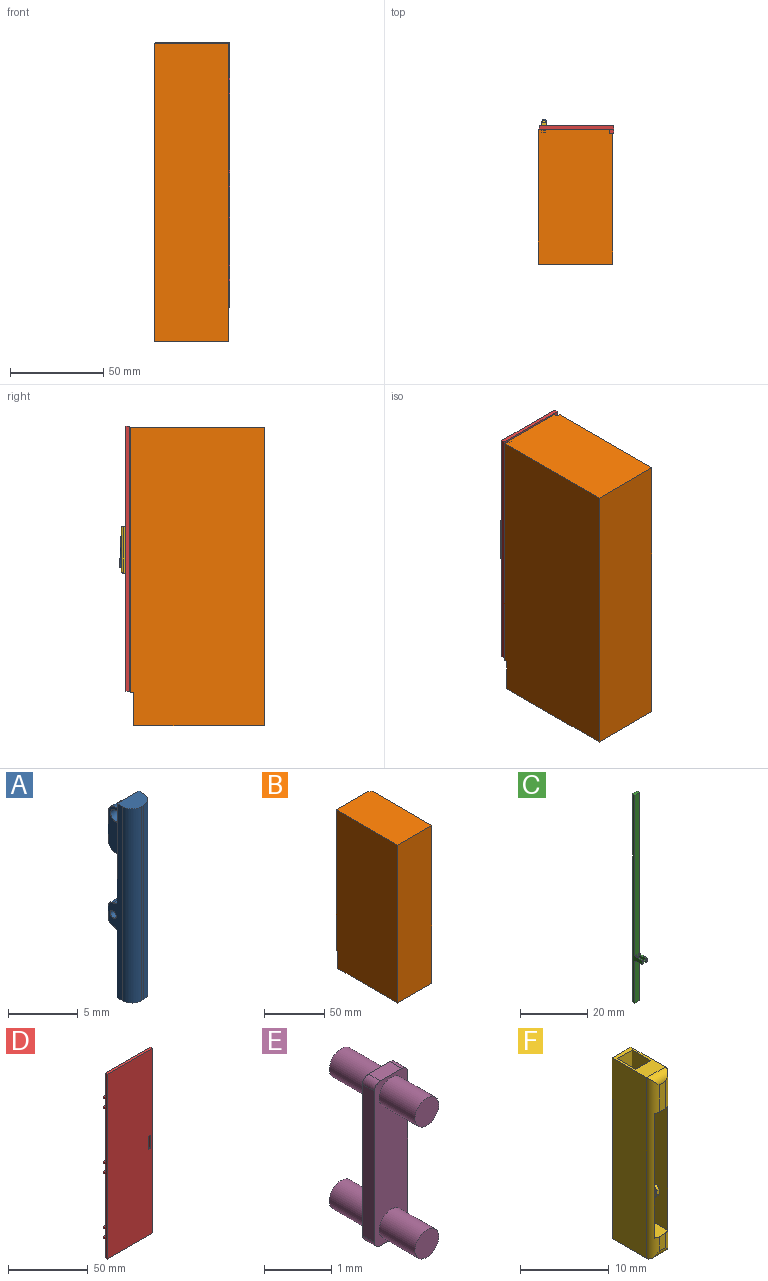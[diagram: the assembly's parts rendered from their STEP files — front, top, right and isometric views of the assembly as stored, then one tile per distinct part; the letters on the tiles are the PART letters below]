
ASSEMBLY  parts=6 mates=5
PART A: 31 faces, bbox 2.2x3x17 mm
  f0: plane 17x0.5mm, normal (1,0,0), area 8.5mm2, adj f2,f4,f29,f30
  f1: plane 17x0.5mm, normal (-1,0,0), area 8.5mm2, adj f2,f4,f28,f30
  f2: plane 2.2x1.5mm, normal (0,0,-1), area 2.9mm2, adj f0,f1,f3,f4,f28,f29
  f3: plane 17x0.2mm, normal (0,-1,0), area 3.4mm2, adj f2,f28,f29,f30
  f4: plane 17x2.2mm, normal (0,1,0), area 29.2mm2, adj f0,f1,f2,f5,f6,f8,f10,f12
  f5: plane 4.75x1.5mm, normal (-1,0,0), area 5mm2, adj f4,f7,f8,f9,f10,f11
  f6: plane 4.75x1.5mm, normal (1,0,0), area 5mm2, adj f4,f7,f8,f9,f10,f11
  f7: plane 2.5x1mm, normal (0,1,0), area 2.5mm2, adj f5,f6,f8,f9
  f8: cylinder r=0.75mm len=1.5mm, axis (-1,0,0), area 2.4mm2, adj f4,f5,f6,f7
  f9: cylinder r=0.75mm len=1mm, axis (1,0,0), area 1.2mm2, adj f5,f6,f7,f10
  f10: cylinder r=0.75mm len=1mm, axis (1,0,0), area 1.2mm2, adj f4,f5,f6,f9
  f11: cylinder r=0.5mm len=1mm, axis (1,0,0), area 3.1mm2, adj f5,f6
  f12: plane 3x1mm, normal (-1,0,0), area 1.7mm2, adj f4,f14,f19,f24,f25,f26,f27
  f13: plane 3x1mm, normal (1,0,0), area 1.7mm2, adj f4,f14,f19,f24,f25,f26,f27
  f14: plane 1x0.7mm, normal (0,1,0), area 0.7mm2, adj f12,f13,f24,f26
  f15: plane 3x1mm, normal (-1,0,0), area 1.7mm2, adj f4,f17,f18,f20,f21,f22,f23
  f16: plane 3x1mm, normal (1,0,0), area 1.7mm2, adj f4,f17,f18,f20,f21,f22,f23
  f17: plane 1x0.7mm, normal (0,1,0), area 0.7mm2, adj f15,f16,f20,f22
  f18: cylinder r=0.3mm len=0.7mm, axis (1,0,0), area 1.3mm2, adj f15,f16
  f19: cylinder r=0.3mm len=0.7mm, axis (1,0,0), area 1.3mm2, adj f12,f13
  f20: cylinder r=0.5mm len=0.7mm, axis (-1,0,0), area 0.5mm2, adj f15,f16,f17,f21
  f21: cylinder r=0.5mm len=0.7mm, axis (-1,0,0), area 0.5mm2, adj f4,f15,f16,f20
  f22: cylinder r=0.5mm len=0.7mm, axis (1,0,0), area 0.5mm2, adj f15,f16,f17,f23
  f23: cylinder r=0.5mm len=0.7mm, axis (1,0,0), area 0.5mm2, adj f4,f15,f16,f22
  f24: cylinder r=0.5mm len=0.7mm, axis (-1,0,0), area 0.5mm2, adj f12,f13,f14,f25
  f25: cylinder r=0.5mm len=0.7mm, axis (-1,0,0), area 0.5mm2, adj f4,f12,f13,f24
  f26: cylinder r=0.5mm len=0.7mm, axis (1,0,0), area 0.5mm2, adj f12,f13,f14,f27
  f27: cylinder r=0.5mm len=0.7mm, axis (1,0,0), area 0.5mm2, adj f4,f12,f13,f26
  f28: cylinder r=1mm len=17mm, axis (0,0,1), area 26.7mm2, adj f1,f2,f3,f30
  f29: cylinder r=1mm len=17mm, axis (0,0,-1), area 26.7mm2, adj f0,f2,f3,f30
  f30: plane 2.2x1.5mm, normal (0,0,1), area 2.9mm2, adj f0,f1,f3,f4,f28,f29
PART B: 38 faces, bbox 40x72x160 mm
  f0: plane 138x70mm, normal (1,0,0), area 9658mm2, adj f1,f12,f13,f35,f36,f37
  f1: plane 69x36mm, normal (0,0,-1), area 2484mm2, adj f0,f11,f13,f32,f36
  f2: plane 40x34mm, normal (0,1,0), area 739mm2, adj f6,f7,f10,f11,f21,f33,f34
  f3: plane 20x2mm, normal (0,1,0), area 40mm2, adj f6,f9,f11,f14,f32
  f4: plane 44x2mm, normal (0,1,0), area 88mm2, adj f6,f11,f18,f20
  f5: plane 44x2mm, normal (0,1,0), area 88mm2, adj f6,f11,f15,f17
  f6: plane 160x71.5mm, normal (1,0,0), area 11227mm2, adj f2,f3,f4,f5,f8,f9,f10,f14
  f7: plane 160x72mm, normal (-1,0,0), area 11484.7mm2, adj f2,f8,f9,f10,f34,f35
  f8: plane 160x40mm, normal (0,-1,0), area 6400mm2, adj f6,f7,f9,f10
  f9: plane 72x40mm, normal (0,0,1), area 2876mm2, adj f3,f6,f7,f8,f32,f35
  f10: plane 70x40mm, normal (0,0,-1), area 2800mm2, adj f2,f6,f7,f8
  f11: plane 138x69.5mm, normal (-1,0,0), area 9411mm2, adj f1,f2,f3,f4,f5,f12,f13,f14
  f12: plane 70x36mm, normal (0,0,1), area 2520mm2, adj f0,f11,f13,f33,f35
  f13: plane 138x36mm, normal (0,1,0), area 4968mm2, adj f0,f1,f11,f12
  f14: plane 2x2mm, normal (0,0,1), area 3.1mm2, adj f3,f6,f11,f16,f27,f28,f31
  f15: plane 2x2mm, normal (0,0,-1), area 3.1mm2, adj f5,f6,f11,f16,f27,f28,f31
  f16: plane 6x1mm, normal (0,1,0), area 6mm2, adj f14,f15,f27,f28
  f17: plane 2x2mm, normal (0,0,1), area 3.1mm2, adj f5,f6,f11,f19,f25,f26,f30
  f18: plane 2x2mm, normal (0,0,-1), area 3.1mm2, adj f4,f6,f11,f19,f25,f26,f30
  f19: plane 6x1mm, normal (0,1,0), area 6mm2, adj f17,f18,f25,f26
  f20: plane 2x2mm, normal (0,0,1), area 3.1mm2, adj f4,f6,f11,f22,f23,f24,f29
  f21: plane 2x2mm, normal (0,0,-1), area 3.1mm2, adj f2,f6,f11,f22,f23,f24,f29
  f22: plane 6x1mm, normal (0,1,0), area 6mm2, adj f20,f21,f23,f24
  f23: cylinder r=0.5mm len=6mm, axis (0,0,-1), area 4.7mm2, adj f6,f20,f21,f22
  f24: cylinder r=0.5mm len=6mm, axis (0,0,1), area 4.7mm2, adj f11,f20,f21,f22
  f25: cylinder r=0.5mm len=6mm, axis (0,0,-1), area 4.7mm2, adj f6,f17,f18,f19
  f26: cylinder r=0.5mm len=6mm, axis (0,0,1), area 4.7mm2, adj f11,f17,f18,f19
  f27: cylinder r=0.5mm len=6mm, axis (0,0,-1), area 4.7mm2, adj f6,f14,f15,f16
  f28: cylinder r=0.5mm len=6mm, axis (0,0,1), area 4.7mm2, adj f11,f14,f15,f16
  f29: cylinder r=0.5mm len=6mm, axis (0,0,1), area 18.8mm2, adj f20,f21
  f30: cylinder r=0.5mm len=6mm, axis (0,0,1), area 18.8mm2, adj f17,f18
  f31: cylinder r=0.5mm len=6mm, axis (0,0,1), area 18.8mm2, adj f14,f15
  f32: plane 4x2mm, normal (1,0,0), area 6mm2, adj f1,f3,f9,f35,f36,f37
  f33: plane 2.34x2mm, normal (1,0,0), area 4.7mm2, adj f2,f12,f34,f35
  f34: plane 38x2mm, normal (0,0,-1), area 76mm2, adj f2,f7,f33,f35
  f35: plane 142.34x38mm, normal (0,1,0), area 513mm2, adj f0,f7,f9,f12,f32,f33,f34,f37
  f36: plane 36x2mm, normal (0,-1,0), area 72mm2, adj f0,f1,f32,f37
  f37: plane 36x1mm, normal (0,0,-1), area 36mm2, adj f0,f32,f35,f36
PART C: 23 faces, bbox 2x4.3x76 mm
  f0: plane 76x2mm, normal (0,-1,0), area 149.8mm2, adj f1,f2,f3,f6,f9,f14,f15,f18
  f1: plane 76x4.25mm, normal (1,0,0), area 80.9mm2, adj f0,f3,f4,f5,f7,f8,f18,f19
  f2: plane 76x4.25mm, normal (-1,0,0), area 80.9mm2, adj f0,f3,f4,f10,f11,f12,f14,f15
  f3: plane 2x1mm, normal (0,0,-1), area 2mm2, adj f0,f1,f2,f4
  f4: plane 76x2mm, normal (0,1,0), area 152mm2, adj f1,f2,f3,f22
  f5: plane 2.25x0.45mm, normal (0,0,1), area 1mm2, adj f1,f6,f18,f20
  f6: plane 3.25x2.5mm, normal (-1,0,0), area 4.7mm2, adj f0,f5,f7,f8,f13,f18,f19,f20
  f7: plane 2.25x0.45mm, normal (0,0,-1), area 1mm2, adj f1,f6,f19,f21
  f8: plane 0.5x0.45mm, normal (0,-1,0), area 0.2mm2, adj f1,f6,f20,f21
  f9: plane 3.25x2.5mm, normal (1,0,0), area 4.7mm2, adj f0,f10,f11,f12,f13,f14,f15,f16
  f10: plane 2.25x0.45mm, normal (0,0,1), area 1mm2, adj f2,f9,f14,f16
  f11: plane 2.25x0.45mm, normal (0,0,-1), area 1mm2, adj f2,f9,f15,f17
  f12: plane 0.5x0.45mm, normal (0,-1,0), area 0.2mm2, adj f2,f9,f16,f17
  f13: cylinder r=0.25mm len=1.1mm, axis (-1,0,0), area 1.7mm2, adj f6,f9
  f14: cylinder r=0.5mm len=0.5mm, axis (-1,0,0), area 0.4mm2, adj f0,f2,f9,f10
  f15: cylinder r=0.5mm len=0.5mm, axis (1,0,0), area 0.4mm2, adj f0,f2,f9,f11
  f16: cylinder r=0.5mm len=0.5mm, axis (1,0,0), area 0.4mm2, adj f2,f9,f10,f12
  f17: cylinder r=0.5mm len=0.5mm, axis (-1,0,0), area 0.4mm2, adj f2,f9,f11,f12
  f18: cylinder r=0.5mm len=0.5mm, axis (-1,0,0), area 0.4mm2, adj f0,f1,f5,f6
  f19: cylinder r=0.5mm len=0.5mm, axis (1,0,0), area 0.4mm2, adj f0,f1,f6,f7
  f20: cylinder r=0.5mm len=0.5mm, axis (1,0,0), area 0.4mm2, adj f1,f5,f6,f8
  f21: cylinder r=0.5mm len=0.5mm, axis (-1,0,0), area 0.4mm2, adj f1,f6,f7,f8
  f22: plane 2x1mm, normal (0,0,1), area 2mm2, adj f0,f1,f2,f4
PART D: 51 faces, bbox 40x4x142 mm
  f0: plane 142x3.5mm, normal (-1,0,0), area 295.2mm2, adj f8,f9,f10,f11,f12,f13,f16,f17
  f1: plane 1.5x1.25mm, normal (1,0,0), area 1.9mm2, adj f11,f12,f29,f35
  f2: plane 2x1.25mm, normal (0,1,0), area 2.5mm2, adj f12,f29,f35,f36
  f3: plane 1.5x1.25mm, normal (1,0,0), area 1.9mm2, adj f11,f16,f26,f37
  f4: plane 2x1.25mm, normal (0,1,0), area 2.5mm2, adj f16,f26,f37,f38
  f5: plane 1.5x1.25mm, normal (1,0,0), area 1.9mm2, adj f11,f20,f24,f39
  f6: plane 2x1.25mm, normal (0,1,0), area 2.5mm2, adj f20,f24,f39,f40
  f7: plane 142x2mm, normal (1,0,0), area 284mm2, adj f8,f9,f10,f11
  f8: plane 40x2mm, normal (0,0,1), area 80mm2, adj f0,f7,f10,f11
  f9: plane 40x2mm, normal (0,0,-1), area 80mm2, adj f0,f7,f10,f11
  f10: plane 142x40mm, normal (0,-1,0), area 5660mm2, adj f0,f7,f8,f9,f47,f48,f49,f50
  f11: plane 142x40mm, normal (0,1,0), area 5637.5mm2, adj f0,f1,f3,f5,f7,f8,f9,f12
  f12: plane 3x2mm, normal (0,0,-1), area 5.1mm2, adj f0,f1,f2,f11,f34,f35,f36
  f13: plane 3x2mm, normal (0,0,1), area 5.9mm2, adj f0,f11,f14,f15,f45,f46
  f14: plane 1.5x1.25mm, normal (1,0,0), area 1.9mm2, adj f11,f13,f28,f46
  f15: plane 2x1.25mm, normal (0,1,0), area 2.5mm2, adj f13,f28,f45,f46
  f16: plane 3x2mm, normal (0,0,-1), area 5.1mm2, adj f0,f3,f4,f11,f33,f37,f38
  f17: plane 3x2mm, normal (0,0,1), area 5.1mm2, adj f0,f11,f18,f19,f34,f43,f44
  f18: plane 1.5x1.25mm, normal (1,0,0), area 1.9mm2, adj f11,f17,f27,f44
  f19: plane 2x1.25mm, normal (0,1,0), area 2.5mm2, adj f17,f27,f43,f44
  f20: plane 3x2mm, normal (0,0,-1), area 5.9mm2, adj f0,f5,f6,f11,f39,f40
  f21: plane 3x2mm, normal (0,0,1), area 5.1mm2, adj f0,f11,f22,f23,f33,f41,f42
  f22: plane 1.5x1.25mm, normal (1,0,0), area 1.9mm2, adj f11,f21,f25,f42
  f23: plane 2x1.25mm, normal (0,1,0), area 2.5mm2, adj f21,f25,f41,f42
  f24: plane 3x2mm, normal (0,0,1), area 5.1mm2, adj f0,f5,f6,f11,f32,f39,f40
  f25: plane 3x2mm, normal (0,0,-1), area 5.1mm2, adj f0,f11,f22,f23,f32,f41,f42
  f26: plane 3x2mm, normal (0,0,1), area 5.1mm2, adj f0,f3,f4,f11,f31,f37,f38
  f27: plane 3x2mm, normal (0,0,-1), area 5.1mm2, adj f0,f11,f18,f19,f31,f43,f44
  f28: plane 3x2mm, normal (0,0,-1), area 5.1mm2, adj f0,f11,f14,f15,f30,f45,f46
  f29: plane 3x2mm, normal (0,0,1), area 5.1mm2, adj f0,f1,f2,f11,f30,f35,f36
  f30: cylinder r=0.5mm len=6.5mm, axis (0,0,1), area 20.4mm2, adj f28,f29
  f31: cylinder r=0.5mm len=6.5mm, axis (0,0,1), area 20.4mm2, adj f26,f27
  f32: cylinder r=0.5mm len=6.5mm, axis (0,0,1), area 20.4mm2, adj f24,f25
  f33: cylinder r=0.5mm len=41mm, axis (0,0,1), area 128.8mm2, adj f16,f21
  f34: cylinder r=0.5mm len=41mm, axis (0,0,1), area 128.8mm2, adj f12,f17
  f35: cylinder r=0.5mm len=1.25mm, axis (0,0,1), area 1mm2, adj f1,f2,f12,f29
  f36: cylinder r=0.5mm len=1.25mm, axis (0,0,1), area 1mm2, adj f0,f2,f12,f29
  f37: cylinder r=0.5mm len=1.25mm, axis (0,0,1), area 1mm2, adj f3,f4,f16,f26
  f38: cylinder r=0.5mm len=1.25mm, axis (0,0,1), area 1mm2, adj f0,f4,f16,f26
  f39: cylinder r=0.5mm len=1.25mm, axis (0,0,1), area 1mm2, adj f5,f6,f20,f24
  f40: cylinder r=0.5mm len=1.25mm, axis (0,0,1), area 1mm2, adj f0,f6,f20,f24
  f41: cylinder r=0.5mm len=1.25mm, axis (0,0,1), area 1mm2, adj f0,f21,f23,f25
  f42: cylinder r=0.5mm len=1.25mm, axis (0,0,1), area 1mm2, adj f21,f22,f23,f25
  f43: cylinder r=0.5mm len=1.25mm, axis (0,0,1), area 1mm2, adj f0,f17,f19,f27
  f44: cylinder r=0.5mm len=1.25mm, axis (0,0,1), area 1mm2, adj f17,f18,f19,f27
  f45: cylinder r=0.5mm len=1.25mm, axis (0,0,1), area 1mm2, adj f0,f13,f15,f28
  f46: cylinder r=0.5mm len=1.25mm, axis (0,0,1), area 1mm2, adj f13,f14,f15,f28
  f47: plane 2x2mm, normal (0,0,-1), area 4mm2, adj f10,f11,f48,f49
  f48: plane 10x2mm, normal (-1,0,0), area 20mm2, adj f10,f11,f47,f50
  f49: plane 10x2mm, normal (1,0,0), area 20mm2, adj f10,f11,f47,f50
  f50: plane 2x2mm, normal (0,0,1), area 4mm2, adj f10,f11,f48,f49
PART E: 18 faces, bbox 0.7x1.8x3 mm
  f0: plane 2.75x0.25mm, normal (1,0,0), area 0.7mm2, adj f1,f7,f8,f9
  f1: cylinder r=0.12mm len=0.25mm, axis (0,1,0), area 0mm2, adj f0,f2,f8,f9
  f2: plane 0.45x0.25mm, normal (0,0,1), area 0.1mm2, adj f1,f3,f8,f9
  f3: cylinder r=0.12mm len=0.25mm, axis (0,1,0), area 0mm2, adj f2,f4,f8,f9
  f4: plane 2.75x0.25mm, normal (-1,0,0), area 0.7mm2, adj f3,f5,f8,f9
  f5: cylinder r=0.12mm len=0.25mm, axis (0,1,0), area 0mm2, adj f4,f6,f8,f9
  f6: plane 0.45x0.25mm, normal (0,0,-1), area 0.1mm2, adj f5,f7,f8,f9
  f7: cylinder r=0.12mm len=0.25mm, axis (0,1,0), area 0mm2, adj f0,f6,f8,f9
  f8: plane 3x0.7mm, normal (0,-1,0), area 1.7mm2, adj f0,f1,f2,f3,f4,f5,f6,f7
  f9: plane 3x0.7mm, normal (0,1,0), area 1.7mm2, adj f0,f1,f2,f3,f4,f5,f6,f7
  f10: plane 0.5x0.5mm, normal (0,1,0), area 0.2mm2, adj f11
  f11: cylinder r=0.25mm len=0.8mm, axis (0,1,0), area 1.3mm2, adj f9,f10
  f12: cylinder r=0.25mm len=0.75mm, axis (0,1,0), area 1.2mm2, adj f8,f13
  f13: plane 0.5x0.5mm, normal (0,-1,0), area 0.2mm2, adj f12
  f14: plane 0.5x0.5mm, normal (0,1,0), area 0.2mm2, adj f15
  f15: cylinder r=0.25mm len=0.8mm, axis (0,1,0), area 1.3mm2, adj f9,f14
  f16: cylinder r=0.25mm len=0.75mm, axis (0,1,0), area 1.2mm2, adj f8,f17
  f17: plane 0.5x0.5mm, normal (0,-1,0), area 0.2mm2, adj f16
PART F: 43 faces, bbox 3x6.5x25 mm
  f0: plane 2x1mm, normal (0,-1,0), area 2mm2, adj f37,f40,f41,f42
  f1: plane 9.5x2.2mm, normal (0,-1,0), area 19.7mm2, adj f8,f9,f13,f15,f16,f17,f18,f20
  f2: plane 2.2x0.5mm, normal (0,0,1), area 1.1mm2, adj f3,f7,f14,f34
  f3: plane 8x0.5mm, normal (1,0,0), area 4mm2, adj f2,f4,f14,f34
  f4: plane 2.2x0.5mm, normal (0,0,-1), area 1.1mm2, adj f3,f7,f14,f34
  f5: plane 5.5x3mm, normal (0,0,1), area 9.3mm2, adj f11,f12,f14,f31,f32,f33,f34,f39
  f6: plane 5.5x3mm, normal (0,0,-1), area 9.3mm2, adj f11,f12,f14,f31,f32,f33,f34,f42
  f7: plane 8x0.5mm, normal (-1,0,0), area 4mm2, adj f2,f4,f14,f34
  f8: plane 2.2x0.5mm, normal (0,0,1), area 1.1mm2, adj f1,f9,f13,f32
  f9: plane 17.5x2.8mm, normal (1,0,0), area 43.7mm2, adj f1,f8,f10,f32,f35,f36,f37,f41
  f10: plane 2.2x0.5mm, normal (0,0,-1), area 1.1mm2, adj f9,f13,f32,f35
  f11: plane 25x5.5mm, normal (1,0,0), area 137.5mm2, adj f5,f6,f14,f40
  f12: plane 25x5.5mm, normal (-1,0,0), area 137.5mm2, adj f5,f6,f14,f41
  f13: plane 17.5x2.8mm, normal (-1,0,0), area 43.7mm2, adj f1,f8,f10,f32,f35,f36,f37,f40
  f14: plane 25x3mm, normal (0,1,0), area 57.4mm2, adj f2,f3,f4,f5,f6,f7,f11,f12
  f15: plane 1.5x1mm, normal (1,0,0), area 1.1mm2, adj f1,f16,f18,f19,f27,f28,f30
  f16: plane 0.5x0.4mm, normal (0,0,1), area 0.2mm2, adj f1,f15,f17,f27
  f17: plane 1.5x1mm, normal (-1,0,0), area 1.1mm2, adj f1,f16,f18,f19,f27,f28,f30
  f18: plane 0.5x0.4mm, normal (0,0,-1), area 0.2mm2, adj f1,f15,f17,f28
  f19: plane 0.5x0.4mm, normal (0,-1,0), area 0.2mm2, adj f15,f17,f27,f28
  f20: plane 1.5x1mm, normal (1,0,0), area 1.1mm2, adj f1,f21,f23,f24,f25,f26,f29
  f21: plane 0.5x0.4mm, normal (0,0,1), area 0.2mm2, adj f1,f20,f22,f25
  f22: plane 1.5x1mm, normal (-1,0,0), area 1.1mm2, adj f1,f21,f23,f24,f25,f26,f29
  f23: plane 0.5x0.4mm, normal (0,0,-1), area 0.2mm2, adj f1,f20,f22,f26
  f24: plane 0.5x0.4mm, normal (0,-1,0), area 0.2mm2, adj f20,f22,f25,f26
  f25: cylinder r=0.5mm len=0.5mm, axis (1,0,0), area 0.3mm2, adj f20,f21,f22,f24
  f26: cylinder r=0.5mm len=0.5mm, axis (-1,0,0), area 0.3mm2, adj f20,f22,f23,f24
  f27: cylinder r=0.5mm len=0.5mm, axis (1,0,0), area 0.3mm2, adj f15,f16,f17,f19
  f28: cylinder r=0.5mm len=0.5mm, axis (-1,0,0), area 0.3mm2, adj f15,f17,f18,f19
  f29: cylinder r=0.3mm len=0.6mm, axis (-1,0,0), area 0.8mm2, adj f20,f22
  f30: cylinder r=0.3mm len=0.6mm, axis (-1,0,0), area 0.8mm2, adj f15,f17
  f31: plane 25x3mm, normal (-1,0,0), area 75mm2, adj f5,f6,f32,f34
  f32: plane 25x2.4mm, normal (0,1,0), area 42.4mm2, adj f5,f6,f8,f9,f10,f13,f31,f33
  f33: plane 25x3mm, normal (1,0,0), area 75mm2, adj f5,f6,f32,f34
  f34: plane 25x2.4mm, normal (0,-1,0), area 42.4mm2, adj f2,f3,f4,f5,f6,f7,f31,f33
  f35: plane 2.2x0.25mm, normal (0,1,0), area 0.6mm2, adj f9,f10,f13,f36
  f36: plane 2.5x2.2mm, normal (0,0,-1), area 5.4mm2, adj f9,f13,f35,f38,f40,f41
  f37: plane 2.5x2.2mm, normal (0,0,1), area 5.4mm2, adj f0,f1,f9,f13,f40,f41
  f38: plane 3.75x1mm, normal (0,-1,0), area 3.7mm2, adj f36,f39,f40,f41
  f39: cylinder r=1mm len=3mm, axis (1,0,0), area 3.6mm2, adj f5,f38,f40,f41
  f40: cylinder r=1mm len=25mm, axis (0,0,-1), area 27mm2, adj f0,f11,f13,f36,f37,f38,f39,f42
  f41: cylinder r=1mm len=25mm, axis (0,0,1), area 27mm2, adj f0,f9,f12,f36,f37,f38,f39,f42
  f42: cylinder r=1mm len=3mm, axis (-1,0,0), area 3.6mm2, adj f0,f6,f40,f41
PLACE A rot(axis=(0,-0.02,1),180deg) t=(-38,52.2,48.74)mm
PLACE B t=(-21.13,11.38,-43.13)mm fixed
PLACE C rot(axis=(0,0,-1),180deg) t=(-38.13,47.13,55.53)mm
PLACE D rot(axis=(0,0,-1),180deg) t=(-20.63,48.63,46.37)mm
PLACE E rot(axis=(-0.11,-0.11,-0.99),90.7deg) t=(-38,51.45,47.54)mm
PLACE F rot(axis=(0,0,-1),180deg) t=(-38.13,46.63,51.12)mm
MATE fastened F.f1 <-> D.f10  axis (0,1,0) through (-38.13,50.63,46.37)mm
MATE revolute B.f29 <-> D.f30  axis (0,0,1) through (-2.13,47.63,96.87)mm
MATE revolute E.f15 <-> F.f29  axis (1,0,0) through (-38.63,51.18,46.37)mm
MATE slider C.f3 <-> F.f6  axis (0,0,-1) through (-38.13,47.63,40.53)mm
MATE revolute A.f18 <-> E.f11  axis (-1,0,0) through (-39,51.72,48.71)mm
